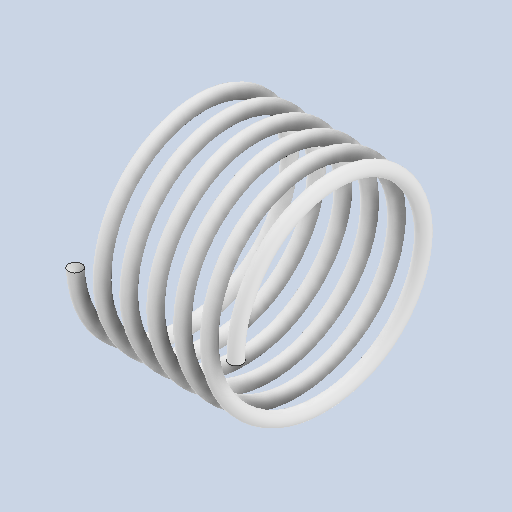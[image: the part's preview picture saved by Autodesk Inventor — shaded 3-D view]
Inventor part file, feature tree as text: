
AUTODESK INVENTOR PART (.ipt)
format: ipt  version: 2022 (Build 260153000, 153)  size: 366,080 bytes
history: native  units: in
note: dims shown in document units (in); Inventor stores cm internally (conversion verified against a paired STEP export)
features: sketch x2, helix x1
ambient origin geometry x8: Origin, YZ Plane, XZ Plane, XY Plane, X Axis, Y Axis, Z Axis, Center Point
bodies: Solid1 (feature_tree)
feature tree (3):
  helix  "Coil1"  [1 undecoded]
  sketch  "Sketch2"
  sketch  "Sketch1"  dims[d3=0.0197in d4=0.3937in d5=2.3622in d6=0.0in d7=90.0deg d8=90.0deg d9=0.0in d10=0.0in d11=0.1575in]
note: 1 required parameter value undecoded (feature->parameter linkage not recoverable at this tier; creation-order binding heuristic only, values carry confidence <= 0.55)
